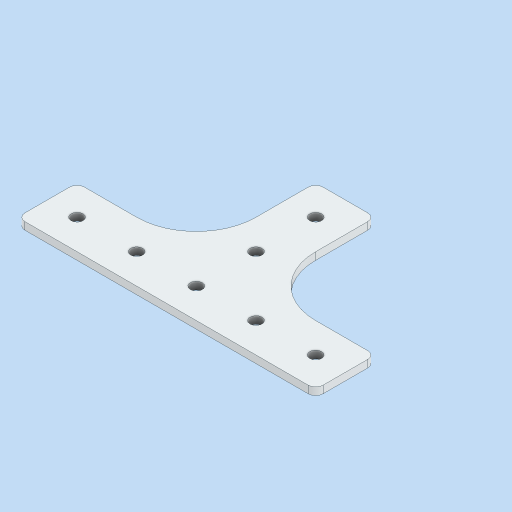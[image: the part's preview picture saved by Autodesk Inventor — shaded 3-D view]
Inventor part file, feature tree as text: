
AUTODESK INVENTOR PART (.ipt)
format: ipt  version: 2024 (Build 280153000, 153)  size: 127,488 bytes
history: native  units: in
note: dims shown in document units (in); Inventor stores cm internally (conversion verified against a paired STEP export)
features: fillet x1
ambient origin geometry x8: Origin, YZ Plane, XZ Plane, XY Plane, X Axis, Y Axis, Z Axis, Center Point
bodies: Solid1 (feature_tree)
feature tree (1):
  fillet  "Fillet2"  [1 undecoded]
note: 1 required parameter value undecoded (feature->parameter linkage not recoverable at this tier; creation-order binding heuristic only, values carry confidence <= 0.55)
